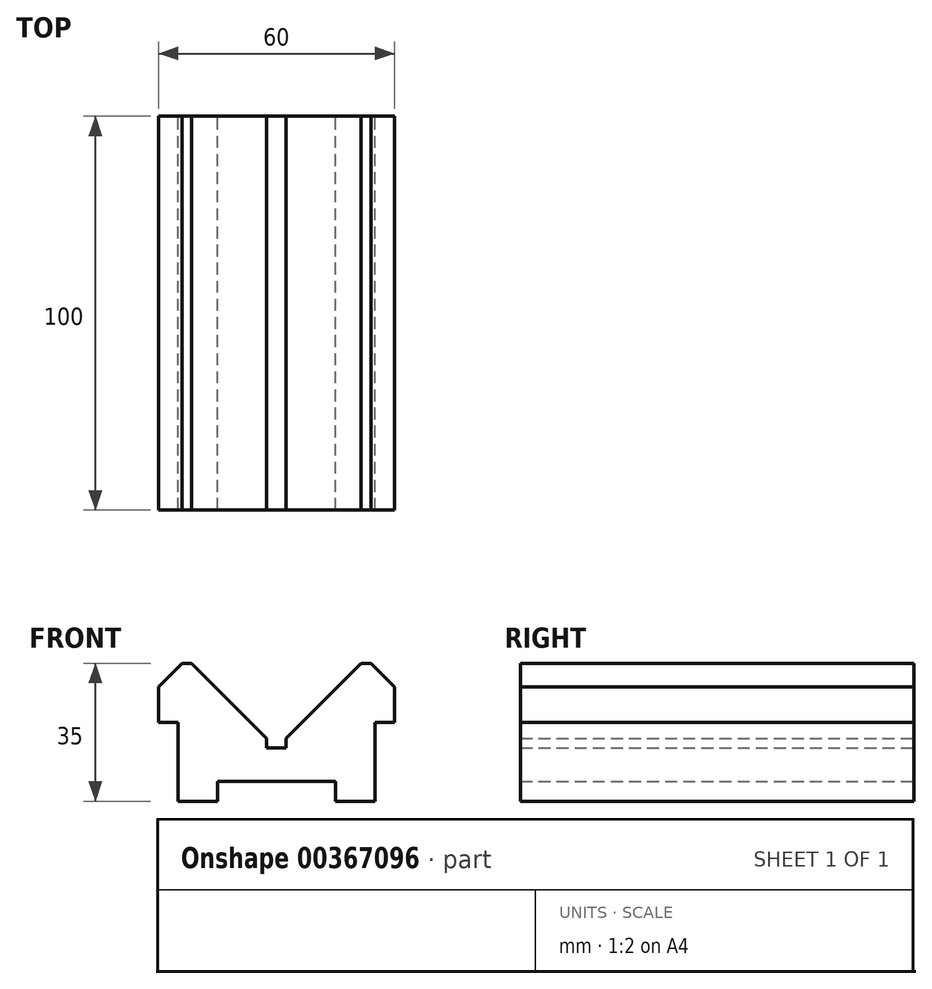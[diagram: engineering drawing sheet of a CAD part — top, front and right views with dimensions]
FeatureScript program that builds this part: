
annotation { "Feature Type Name" : "Feature", "Feature Type Description" : "" }
export const myFeature = defineFeature(function(context is Context, id is Id, definition is map)
    precondition{}
    {
        {
            var Q0;
            Q0=qCreatedBy(makeId("Front.planeOp"),FACE);
            var sketch = newSketch(context, id + "F0", { "sketchPlane" : qUnion([Q0])});
            skLineSegment(sketch, "E0", {"start": v(0, 0) * mm, "end": v(30, 0) * mm, "construction": true});
            skLineSegment(sketch, "E1", {"start": v(30, 0) * mm, "end": v(30, 35) * mm, "construction": true});
            skLineSegment(sketch, "E2.MirrorCS", {"start": v(0, 0) * mm, "end": v(-30, 0) * mm, "construction": true});
            skLineSegment(sketch, "E3.MirrorCS", {"start": v(-30, 0) * mm, "end": v(-30, 35) * mm, "construction": true});
            skLineSegment(sketch, "E4", {"start": v(-30, 35) * mm, "end": v(30, 35) * mm, "construction": true});
            skLineSegment(sketch, "E5", {"start": v(-30, 35) * mm, "end": v(-21.5, 35) * mm, "construction": true});
            skLineSegment(sketch, "E6", {"start": v(0, 13.5) * mm, "end": v(-2.5, 13.5) * mm});
            skLineSegment(sketch, "E7", {"start": v(-2.5, 13.5) * mm, "end": v(-2.5, 16) * mm});
            skLineSegment(sketch, "E8", {"start": v(-21.5, 35) * mm, "end": v(-2.5, 16) * mm});
            skLineSegment(sketch, "E9", {"start": v(-21.5, 35) * mm, "end": v(-24, 35) * mm});
            skLineSegment(sketch, "E10", {"start": v(0, 0) * mm, "end": v(0, 5) * mm, "construction": true});
            skLineSegment(sketch, "E11", {"start": v(0, 5) * mm, "end": v(-15, 5) * mm});
            skLineSegment(sketch, "E12", {"start": v(-15, 5) * mm, "end": v(-15, 0) * mm});
            skLineSegment(sketch, "E13", {"start": v(-15, 0) * mm, "end": v(-25, 0) * mm});
            skLineSegment(sketch, "E14", {"start": v(-25, 0) * mm, "end": v(-25, 20) * mm});
            skLineSegment(sketch, "E15", {"start": v(-25, 20) * mm, "end": v(-30, 20) * mm});
            skLineSegment(sketch, "E16", {"start": v(-30, 20) * mm, "end": v(-30, 29) * mm});
            skLineSegment(sketch, "E17", {"start": v(-30, 29) * mm, "end": v(-24, 35) * mm});
            skLineSegment(sketch, "E18.MirrorCS", {"start": v(0, 13.5) * mm, "end": v(2.5, 13.5) * mm});
            skLineSegment(sketch, "E19.MirrorCS", {"start": v(21.5, 35) * mm, "end": v(2.5, 16) * mm});
            skLineSegment(sketch, "E20.MirrorCS", {"start": v(2.5, 13.5) * mm, "end": v(2.5, 16) * mm});
            skLineSegment(sketch, "E21.MirrorCS", {"start": v(21.5, 35) * mm, "end": v(24, 35) * mm});
            skLineSegment(sketch, "E22.MirrorCS", {"start": v(30, 29) * mm, "end": v(24, 35) * mm});
            skLineSegment(sketch, "E23.MirrorCS", {"start": v(30, 20) * mm, "end": v(30, 29) * mm});
            skLineSegment(sketch, "E24.MirrorCS", {"start": v(25, 20) * mm, "end": v(30, 20) * mm});
            skLineSegment(sketch, "E25.MirrorCS", {"start": v(25, 0) * mm, "end": v(25, 20) * mm});
            skLineSegment(sketch, "E26.MirrorCS", {"start": v(15, 0) * mm, "end": v(25, 0) * mm});
            skLineSegment(sketch, "E27.MirrorCS", {"start": v(15, 5) * mm, "end": v(15, 0) * mm});
            skLineSegment(sketch, "E28.MirrorCS", {"start": v(0, 5) * mm, "end": v(15, 5) * mm});
            skSolve(sketch);
        }
        {
            var Q0;
            Q0=makeQuery(id+"F0.imprint","IMPRINT",FACE,{"disambiguationData":[TD([[makeQuery(id+"F0.imprint","IMPRINT",EDGE,{"derivedFrom":sQuery(id+"F0.wireOp",EDGE,"E6")}),1.0]])]});
            extrude(context, id + "F1", {"entities" : qUnion([Q0]), "depth" : 100 * mm});
        }
    });
